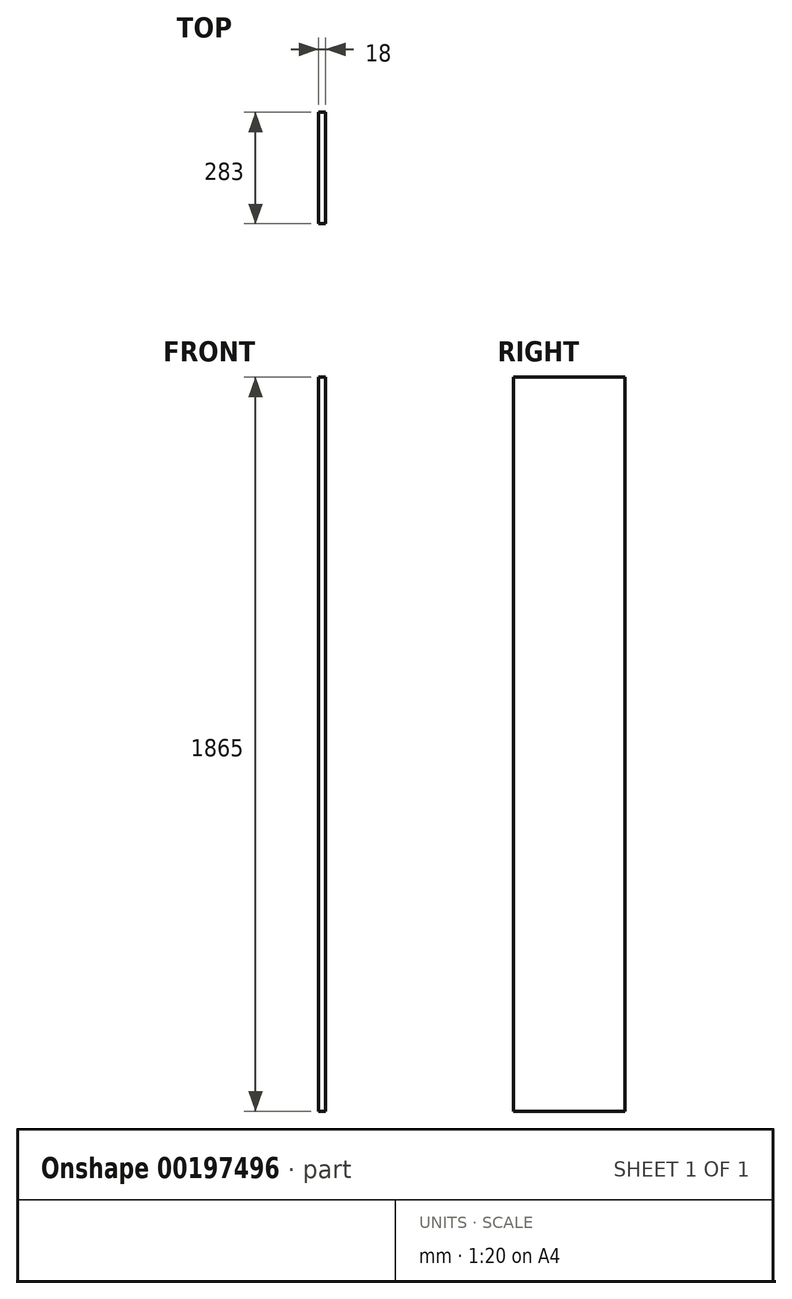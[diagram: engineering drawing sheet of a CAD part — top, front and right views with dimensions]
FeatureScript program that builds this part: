
annotation { "Feature Type Name" : "Feature", "Feature Type Description" : "" }
export const myFeature = defineFeature(function(context is Context, id is Id, definition is map)
    precondition{}
    {
        {
            var Q0;
            Q0=qCreatedBy(makeId("Right.planeOp"),FACE);
            var sketch = newSketch(context, id + "F0", { "sketchPlane" : qUnion([Q0])});
            skLineSegment(sketch, "E0.bottom", {"start": v(141.5, 932.5) * mm, "end": v(-141.5, 932.5) * mm});
            skLineSegment(sketch, "E0.top", {"start": v(141.5, -932.5) * mm, "end": v(-141.5, -932.5) * mm});
            skLineSegment(sketch, "E0.left", {"start": v(141.5, 932.5) * mm, "end": v(141.5, -932.5) * mm});
            skLineSegment(sketch, "E0.right", {"start": v(-141.5, 932.5) * mm, "end": v(-141.5, -932.5) * mm});
            skPoint(sketch, "E0.middle", {"position": v(0, 0) * mm});
            skSolve(sketch);
        }
        {
            var Q0;
            Q0 = qSketchRegion(id + "F0", true);
            extrude(context, id + "F1", {"entities" : qUnion([Q0]), "depth" : 18 * mm});
        }
    });
